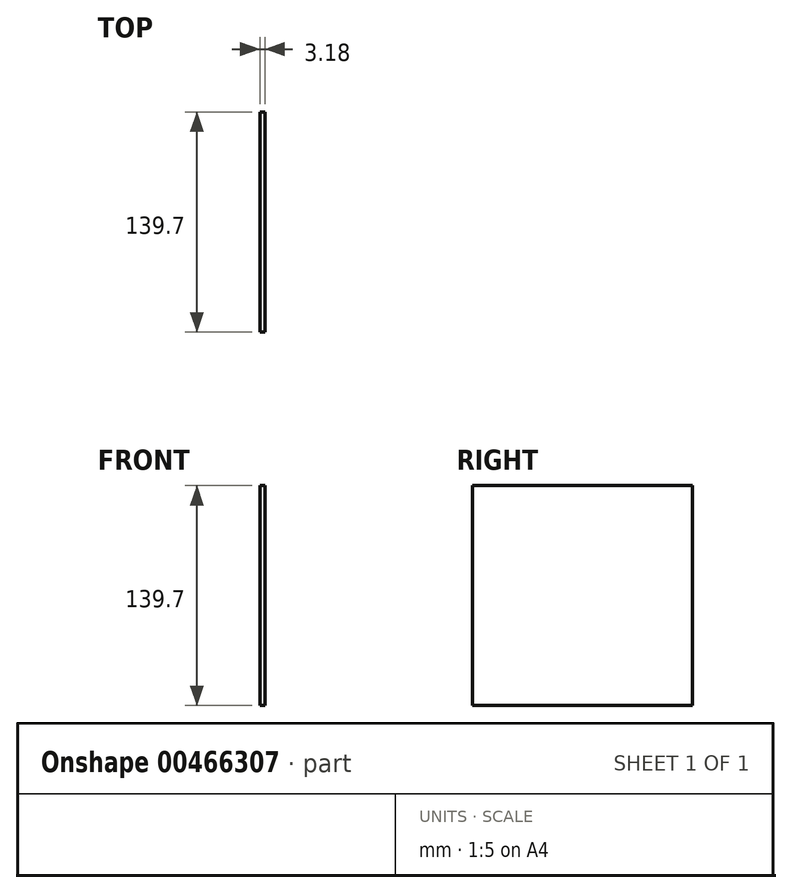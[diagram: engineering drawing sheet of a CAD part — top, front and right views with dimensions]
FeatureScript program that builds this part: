
annotation { "Feature Type Name" : "Feature", "Feature Type Description" : "" }
export const myFeature = defineFeature(function(context is Context, id is Id, definition is map)
    precondition{}
    {
        {
            var Q0;
            Q0=qCreatedBy(makeId("Front.planeOp"),FACE);
            var sketch = newSketch(context, id + "F0", { "sketchPlane" : qUnion([Q0])});
            skLineSegment(sketch, "E0", {"start": v(-45.8, 77.77) * mm, "end": v(-45.8, -61.93) * mm});
            skLineSegment(sketch, "E1", {"start": v(-45.8, -61.93) * mm, "end": v(-48.97, -61.93) * mm});
            skLineSegment(sketch, "E2", {"start": v(-48.97, 77.77) * mm, "end": v(-48.97, -61.93) * mm});
            skLineSegment(sketch, "E3", {"start": v(-45.8, 77.77) * mm, "end": v(-48.97, 77.77) * mm});
            skSolve(sketch);
        }
        {
            var Q0;
            Q0=makeQuery(id+"F0.imprint","IMPRINT",FACE,{"disambiguationData":[TD([[makeQuery(id+"F0.imprint","IMPRINT",EDGE,{"derivedFrom":sQuery(id+"F0.wireOp",EDGE,"E0")}),-1.0]])]});
            extrude(context, id + "F1", {"entities" : qUnion([Q0]), "depth" : 139.7 * mm});
        }
    });
